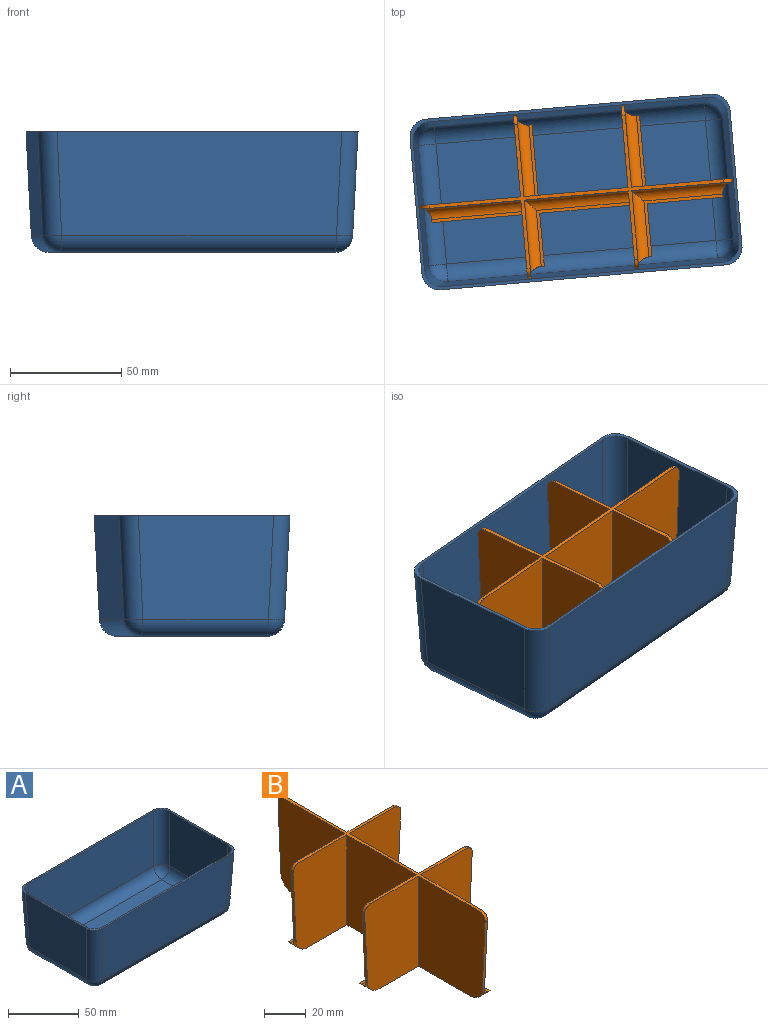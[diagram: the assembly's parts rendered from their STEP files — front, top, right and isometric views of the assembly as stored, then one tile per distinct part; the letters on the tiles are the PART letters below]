
ASSEMBLY  parts=2 mates=1
PART A: 35 faces, bbox 144.6x77.1x54.5 mm
  f0: plane 61.12x46.68mm, normal (1,0,-0.05), area 2753.1mm2, adj f8,f13,f16,f26
  f1: plane 128.62x46.68mm, normal (0,1,-0.05), area 5907.3mm2, adj f8,f13,f14,f22
  f2: plane 61.12x46.68mm, normal (-1,0,-0.05), area 2753.1mm2, adj f8,f14,f15,f19
  f3: plane 58.52x45.38mm, normal (1,0,0.05), area 2561.1mm2, adj f8,f9,f12,f32
  f4: plane 126.02x45.38mm, normal (0,-1,0.05), area 5627.4mm2, adj f8,f9,f10,f28
  f5: plane 58.52x45.38mm, normal (-1,0,0.05), area 2561.1mm2, adj f8,f10,f11,f29
  f6: plane 126.02x45.38mm, normal (0,1,0.05), area 5627.4mm2, adj f8,f11,f12,f33
  f7: plane 128.62x46.68mm, normal (0,-1,-0.05), area 5907.3mm2, adj f8,f15,f16,f23
  f8: plane 144.6x77.1mm, normal (0,0,1), area 569.7mm2, adj f0,f1,f2,f3,f4,f5,f6,f7
  f9: cylinder r=8mm len=45.69mm, axis (0.05,-0.05,-1), area 572mm2, adj f3,f4,f8,f30
  f10: cylinder r=8mm len=45.69mm, axis (-0.05,-0.05,-1), area 572mm2, adj f4,f5,f8,f27
  f11: cylinder r=8mm len=45.69mm, axis (-0.05,0.05,-1), area 572mm2, adj f5,f6,f8,f31
  f12: cylinder r=8mm len=45.69mm, axis (0.05,0.05,-1), area 572mm2, adj f3,f6,f8,f34
  f13: cylinder r=8mm len=46.99mm, axis (0.05,0.05,1), area 588.3mm2, adj f0,f1,f8,f24
  f14: cylinder r=8mm len=46.99mm, axis (-0.05,0.05,1), area 588.3mm2, adj f1,f2,f8,f20
  f15: cylinder r=8mm len=46.99mm, axis (-0.05,-0.05,1), area 588.3mm2, adj f2,f7,f8,f21
  f16: cylinder r=8mm len=46.99mm, axis (0.05,-0.05,1), area 588.3mm2, adj f0,f7,f8,f25
  f17: plane 121.74x54.24mm, normal (0,0,1), area 6602.8mm2, adj f28,f29,f32,f33
  f18: plane 124.22x56.72mm, normal (0,0,-1), area 7044.9mm2, adj f19,f22,f23,f26
  f19: cylinder r=8mm len=56.72mm, axis (0,1,0), area 691.3mm2, adj f2,f18,f20,f21
  f20: sphere r=8mm, area 94.5mm2, adj f14,f19,f22
  f21: sphere r=8mm, area 94.5mm2, adj f15,f19,f23
  f22: cylinder r=8mm len=124.22mm, axis (1,0,0), area 1514.1mm2, adj f1,f18,f20,f24
  f23: cylinder r=8mm len=124.22mm, axis (1,0,0), area 1514.1mm2, adj f7,f18,f21,f25
  f24: sphere r=8mm, area 94.5mm2, adj f13,f22,f26
  f25: sphere r=8mm, area 94.5mm2, adj f16,f23,f26
  f26: cylinder r=8mm len=56.72mm, axis (0,-1,0), area 691.3mm2, adj f0,f18,f24,f25
  f27: sphere r=8mm, area 94.5mm2, adj f10,f28,f29
  f28: cylinder r=8mm len=121.74mm, axis (-1,0,0), area 1483.9mm2, adj f4,f17,f27,f30
  f29: cylinder r=8mm len=54.24mm, axis (0,-1,0), area 661.1mm2, adj f5,f17,f27,f31
  f30: sphere r=8mm, area 94.5mm2, adj f9,f28,f32
  f31: sphere r=8mm, area 94.5mm2, adj f11,f29,f33
  f32: cylinder r=8mm len=54.24mm, axis (0,-1,0), area 661.1mm2, adj f3,f17,f30,f34
  f33: cylinder r=8mm len=121.74mm, axis (-1,0,0), area 1483.9mm2, adj f6,f17,f31,f34
  f34: sphere r=8mm, area 94.5mm2, adj f12,f32,f33
PART B: 53 faces, bbox 73.1x140.8x53 mm
  f0: plane 40.6x2mm, normal (1,0,0), area 81.2mm2, adj f8,f11,f23,f30
  f1: plane 40.66x2mm, normal (1,0,0), area 78mm2, adj f2,f11,f32,f39
  f2: plane 40.66x1.4mm, normal (0,0,1), area 56.9mm2, adj f1,f32,f39,f40
  f3: plane 47x46mm, normal (1,0,0), area 2162mm2, adj f13,f23,f31,f43
  f4: plane 46x45.31mm, normal (1,0,0), area 2039.3mm2, adj f13,f14,f32,f39,f40,f52
  f5: plane 53x47mm, normal (-1,0,0), area 2472.8mm2, adj f11,f13,f20,f26,f27,f28,f45
  f6: plane 53x45.31mm, normal (-1,0,0), area 2329.1mm2, adj f11,f13,f14,f29,f39,f52
  f7: plane 34.26x2mm, normal (1,0,0), area 65.2mm2, adj f11,f12,f21,f38
  f8: plane 42x25.31mm, normal (0,0,1), area 92.3mm2, adj f0,f23,f30,f35,f43,f44
  f9: plane 46x45.31mm, normal (1,0,0), area 2039.3mm2, adj f13,f15,f22,f38,f41,f51
  f10: plane 53x45.31mm, normal (-1,0,0), area 2311mm2, adj f11,f13,f15,f17,f18,f19,f38,f46
  f11: plane 120.94x53.24mm, normal (0,0,-1), area 1691.3mm2, adj f0,f1,f5,f6,f7,f10,f19,f20
  f12: plane 35.66x25.31mm, normal (0,0,1), area 83.4mm2, adj f7,f21,f37,f38,f41,f42
  f13: plane 132.81x65.11mm, normal (0,0,1), area 415.7mm2, adj f3,f4,f5,f6,f9,f10,f17,f20
  f14: plane 41.19x1.94mm, normal (0,-1,-0.05), area 66mm2, adj f4,f6,f39,f52
  f15: plane 41.19x1.94mm, normal (0,1,-0.05), area 66mm2, adj f9,f10,f38,f51
  f16: plane 41.19x1.94mm, normal (-1,0,-0.05), area 66mm2, adj f17,f20,f36,f49
  f17: plane 46x36.56mm, normal (0,1,0), area 1636.8mm2, adj f10,f13,f16,f36,f46,f49
  f18: plane 31.91x1.4mm, normal (0,0,1), area 44.7mm2, adj f10,f19,f36,f46
  f19: plane 31.91x2mm, normal (0,1,0), area 60.5mm2, adj f10,f11,f18,f36
  f20: plane 53x36.56mm, normal (0,-1,0), area 1865.4mm2, adj f5,f11,f13,f16,f36,f49
  f21: plane 23.91x2mm, normal (0,1,0), area 44.5mm2, adj f7,f11,f12,f37
  f22: plane 46x34.96mm, normal (0,1,0), area 1563.2mm2, adj f9,f13,f24,f37,f42,f50
  f23: plane 53x34.96mm, normal (0,-1,0), area 1762.4mm2, adj f0,f3,f8,f11,f13,f24,f37,f43
  f24: plane 41.19x1.94mm, normal (1,0,-0.05), area 66mm2, adj f22,f23,f37,f50
  f25: plane 41.19x1.94mm, normal (-1,0,-0.05), area 66mm2, adj f26,f29,f34,f47
  f26: plane 46x36.56mm, normal (0,1,0), area 1636.8mm2, adj f5,f13,f25,f34,f45,f47
  f27: plane 31.91x1.4mm, normal (0,0,1), area 44.7mm2, adj f5,f28,f34,f45
  f28: plane 31.91x2mm, normal (0,1,0), area 60.5mm2, adj f5,f11,f27,f34
  f29: plane 53x36.56mm, normal (0,-1,0), area 1865.4mm2, adj f6,f11,f13,f25,f34,f47
  f30: plane 23.91x2mm, normal (0,1,0), area 44.5mm2, adj f0,f8,f11,f35
  f31: plane 46x34.96mm, normal (0,1,0), area 1563.2mm2, adj f3,f13,f33,f35,f44,f48
  f32: plane 53x34.96mm, normal (0,-1,0), area 1762.4mm2, adj f1,f2,f4,f11,f13,f33,f35,f40
  f33: plane 41.19x1.94mm, normal (1,0,-0.05), area 66mm2, adj f31,f32,f35,f48
  f34: cylinder r=8mm len=8mm, axis (0,1,0), area 63.5mm2, adj f11,f25,f26,f27,f28,f29,f45
  f35: cylinder r=8mm len=8mm, axis (0,1,0), area 63.5mm2, adj f8,f11,f30,f31,f32,f33,f44
  f36: cylinder r=8mm len=8mm, axis (0,1,0), area 63.5mm2, adj f11,f16,f17,f18,f19,f20,f46
  f37: cylinder r=8mm len=8mm, axis (0,1,0), area 63.5mm2, adj f11,f12,f21,f22,f23,f24,f42
  f38: cylinder r=8mm len=8mm, axis (1,0,0), area 63.5mm2, adj f7,f9,f10,f11,f12,f15,f41
  f39: cylinder r=8mm len=8mm, axis (1,0,0), area 63.5mm2, adj f1,f2,f4,f6,f11,f14,f40
  f40: cylinder r=5mm len=43.31mm, axis (0,1,0), area 329.5mm2, adj f2,f4,f32,f39
  f41: cylinder r=5mm len=43.31mm, axis (0,1,0), area 315.2mm2, adj f9,f12,f38,f42
  f42: cylinder r=5mm len=32.96mm, axis (-1,0,0), area 233.9mm2, adj f12,f22,f37,f41
  f43: cylinder r=5mm len=47mm, axis (0,1,0), area 354.9mm2, adj f3,f8,f23,f44
  f44: cylinder r=5mm len=32.96mm, axis (-1,0,0), area 233.9mm2, adj f8,f31,f35,f43
  f45: cylinder r=5mm len=34.56mm, axis (-1,0,0), area 260.8mm2, adj f5,f26,f27,f34
  f46: cylinder r=5mm len=34.56mm, axis (-1,0,0), area 260.8mm2, adj f10,f17,f18,f36
  f47: cylinder r=4mm len=4.19mm, axis (0,-1,0), area 10.4mm2, adj f13,f25,f26,f29
  f48: cylinder r=4mm len=4.19mm, axis (0,-1,0), area 10.4mm2, adj f13,f31,f32,f33
  f49: cylinder r=4mm len=4.19mm, axis (0,-1,0), area 10.4mm2, adj f13,f16,f17,f20
  f50: cylinder r=4mm len=4.19mm, axis (0,-1,0), area 10.4mm2, adj f13,f22,f23,f24
  f51: cylinder r=4mm len=4.19mm, axis (-1,0,0), area 10.4mm2, adj f9,f10,f13,f15
  f52: cylinder r=4mm len=4.19mm, axis (-1,0,0), area 10.4mm2, adj f4,f6,f13,f14
PLACE A rot(axis=(0,0,1),5deg) t=(-0.85,4.73,-15.91)mm
PLACE B rot(axis=(0,0,-1),85deg) t=(-0.85,4.73,-15.91)mm
MATE revolute B.f11 <-> A.f17  axis (0,0,1) through (-0.85,4.73,-15.91)mm
